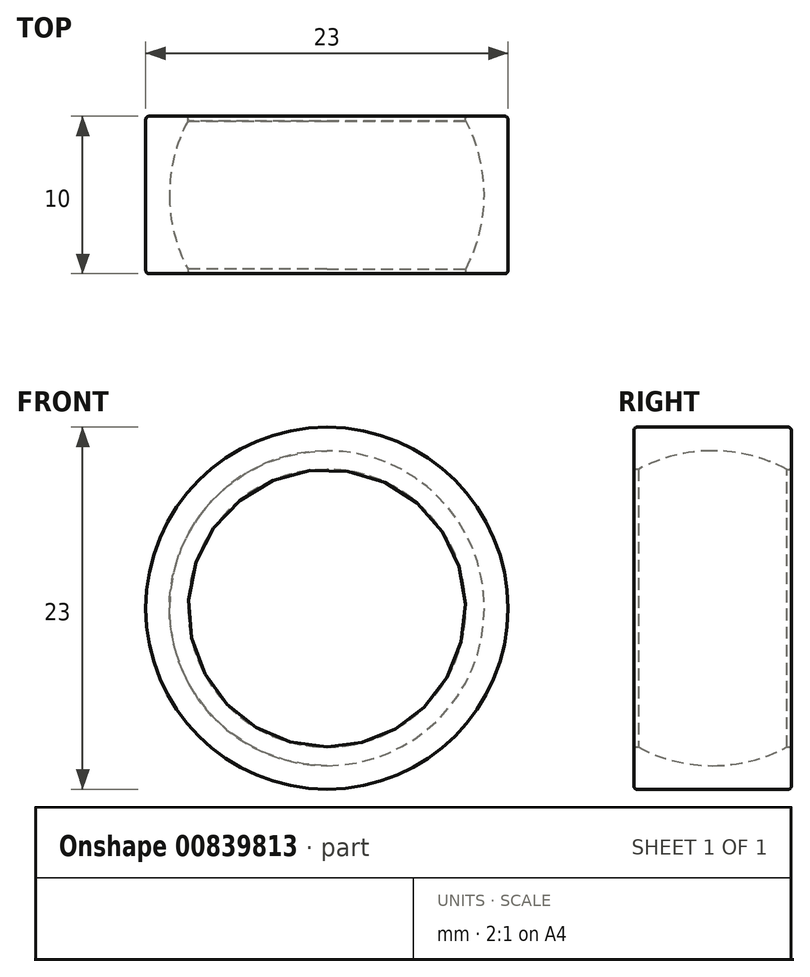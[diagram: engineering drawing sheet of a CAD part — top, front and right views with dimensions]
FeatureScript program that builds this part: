
annotation { "Feature Type Name" : "Feature", "Feature Type Description" : "" }
export const myFeature = defineFeature(function(context is Context, id is Id, definition is map)
    precondition{}
    {
        {
            var Q0;
            Q0=qCreatedBy(makeId("Front.planeOp"),FACE);
            var sketch = newSketch(context, id + "F0", { "sketchPlane" : qUnion([Q0])});
            skCircle(sketch, "E0", {"center": v(0, 0) * mm, "radius": 11.5 * mm});
            skSolve(sketch);
        }
        {
            var Q0;
            Q0=makeQuery(id+"F0.imprint","IMPRINT",FACE,{"disambiguationData":[TD([[makeQuery(id+"F0.imprint","IMPRINT",EDGE,{"derivedFrom":sQuery(id+"F0.wireOp",EDGE,"E0")}),1.0]])]});
            var Q1;
            Q1=sQuery(id+"F0.wireOp",EDGE,"E0");
            extrude(context, id + "F1", {"entities" : qUnion([Q0]), "surfaceEntities" : qUnion([Q1]), "depth" : 5 * mm, "offsetDistance" : 25 * mm, "hasSecondDirection" : true, "secondDirectionOppositeDirection" : true, "secondDirectionDepth" : 5 * mm});
        }
        {
            var Q0;
            Q0=makeQuery(id+"F1.opExtrude","CAP_EDGE",EDGE,{"disambiguationData":[OSD([sQuery(id+"F0.wireOp",EDGE,"E0")])],"isStart":false});
            var Q1;
            Q1=makeQuery(id+"F1.opExtrude","CAP_EDGE",EDGE,{"disambiguationData":[OSD([sQuery(id+"F0.wireOp",EDGE,"E0")])],"isStart":true});
            fillet(context, id + "F2", {"entities" : qUnion([Q0, Q1]), "radius" : 0.2 * mm, "tangentPropagation" : true, "allowEdgeOverflow" : false});
        }
        {
            var Q0;
            Q0=qCreatedBy(makeId("Front.planeOp"),FACE);
            var sketch = newSketch(context, id + "F3", { "sketchPlane" : qUnion([Q0])});
            skArc(sketch, "E1", {"start": v(0, 10) * mm, "mid": v(-10, 0) * mm, "end": v(0, -10) * mm});
            skLineSegment(sketch, "E2", {"start": v(0, -10) * mm, "end": v(0, 10) * mm});
            skSolve(sketch);
        }
        {
            var Q0;
            Q0 = qSketchRegion(id + "F3", true);
            var Q1;
            Q1=sQuery(id+"F3.wireOp",EDGE,"E2");
            revolve(context, id + "F4", {"operationType" : NewBodyOperationType.REMOVE, "surfaceOperationType" : NewSurfaceOperationType.NEW, "entities" : qUnion([Q0]), "axis" : qUnion([Q1]), "revolveType" : RevolveType.FULL, "oppositeDirection" : true});
        }
        {
            var Q0;
            Q0=makeQuery(id+"F4.boolean.opBoolean","INTERSECT",EDGE,{"derivedFrom":[makeQuery(id+"F1.opExtrude","CAP_FACE",FACE,{"disambiguationData":[OSD([sQuery(id+"F0.wireOp",EDGE,"E0")])],"isStart":true}),makeQuery(id+"F4.opRevolve","SWEPT_FACE",FACE,{"disambiguationData":[OSD([sQuery(id+"F3.wireOp",EDGE,"E1")])]})]});
            var Q1;
            Q1=makeQuery(id+"F4.boolean.opBoolean","INTERSECT",EDGE,{"derivedFrom":[makeQuery(id+"F1.opExtrude","CAP_FACE",FACE,{"disambiguationData":[OSD([sQuery(id+"F0.wireOp",EDGE,"E0")])],"isStart":false}),makeQuery(id+"F4.opRevolve","SWEPT_FACE",FACE,{"disambiguationData":[OSD([sQuery(id+"F3.wireOp",EDGE,"E1")])]})]});
            fillet(context, id + "F5", {"entities" : qUnion([Q0, Q1]), "radius" : 0.2 * mm, "tangentPropagation" : true, "allowEdgeOverflow" : false});
        }
    });
